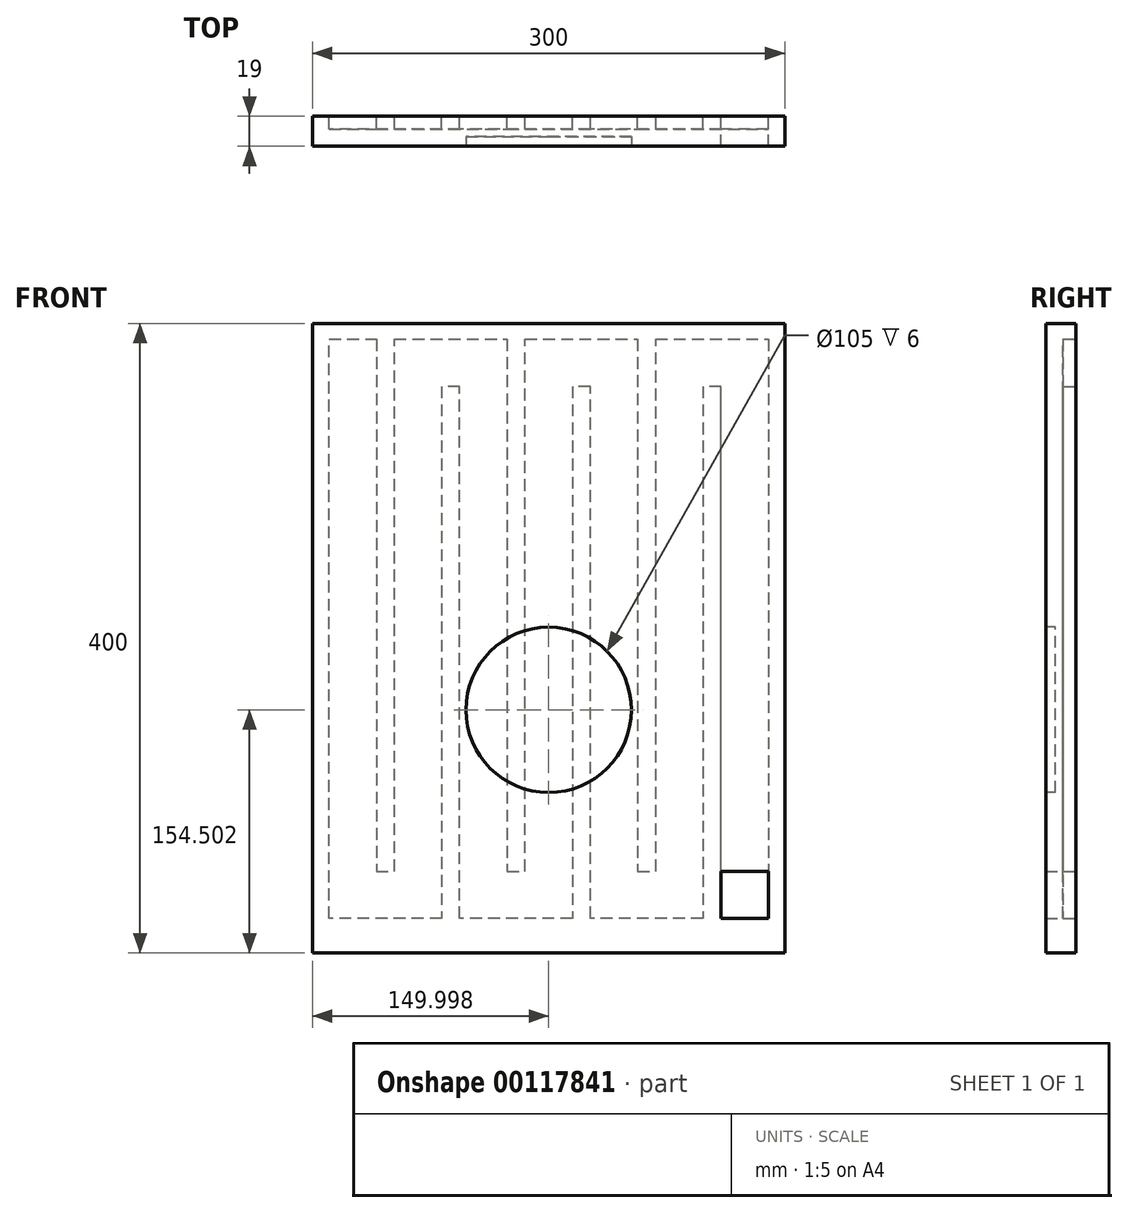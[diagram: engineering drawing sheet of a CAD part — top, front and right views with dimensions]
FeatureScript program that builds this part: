
annotation { "Feature Type Name" : "Feature", "Feature Type Description" : "" }
export const myFeature = defineFeature(function(context is Context, id is Id, definition is map)
    precondition{}
    {
        {
            var Q0;
            Q0=qCreatedBy(makeId("Front.planeOp"),FACE);
            var sketch = newSketch(context, id + "F0", { "sketchPlane" : qUnion([Q0])});
            skLineSegment(sketch, "E0.bottom", {"start": v(-198.08, 243.93) * mm, "end": v(101.92, 243.93) * mm});
            skLineSegment(sketch, "E0.top", {"start": v(-198.08, -156.07) * mm, "end": v(101.92, -156.07) * mm});
            skLineSegment(sketch, "E0.left", {"start": v(-198.08, 243.93) * mm, "end": v(-198.08, -156.07) * mm});
            skLineSegment(sketch, "E0.right", {"start": v(101.92, 243.93) * mm, "end": v(101.92, -156.07) * mm});
            skSolve(sketch);
        }
        {
            var Q0;
            Q0 = qSketchRegion(id + "F0", true);
            extrude(context, id + "F1", {"entities" : qUnion([Q0]), "depth" : 19 * mm});
        }
        {
            var Q0;
            Q0=makeQuery(id+"F1.opExtrude","CAP_FACE",FACE,{"disambiguationData":[OSD([sQuery(id+"F0.wireOp",EDGE,"E0.bottom"),sQuery(id+"F0.wireOp",EDGE,"E0.top"),sQuery(id+"F0.wireOp",EDGE,"E0.left"),sQuery(id+"F0.wireOp",EDGE,"E0.right")])],"isStart":false});
            var sketch = newSketch(context, id + "F2", { "sketchPlane" : qUnion([Q0])});
            skCircle(sketch, "E1", {"center": v(-48.08, -1.57) * mm, "radius": 52.5 * mm});
            skPoint(sketch, "E1.centerSnap0", {"position": v(-48.08, -156.07) * mm});
            skSolve(sketch);
        }
        {
            var Q0;
            Q0=makeQuery(id+"F2.imprint","IMPRINT",FACE,{"disambiguationData":[TD([[makeQuery(id+"F2.imprint","IMPRINT",EDGE,{"derivedFrom":sQuery(id+"F2.wireOp",EDGE,"E1")}),1.0]])]});
            extrude(context, id + "F3", {"entities" : qUnion([Q0]), "operationType" : NewBodyOperationType.REMOVE, "oppositeDirection" : true, "depth" : 6 * mm});
        }
        {
            var Q0;
            Q0=makeQuery(id+"F1.opExtrude","CAP_FACE",FACE,{"disambiguationData":[OSD([sQuery(id+"F0.wireOp",EDGE,"E0.bottom"),sQuery(id+"F0.wireOp",EDGE,"E0.top"),sQuery(id+"F0.wireOp",EDGE,"E0.left"),sQuery(id+"F0.wireOp",EDGE,"E0.right")])],"isStart":true});
            var sketch = newSketch(context, id + "F4", { "sketchPlane" : qUnion([Q0])});
            skLineSegment(sketch, "E2", {"start": v(-91.42, -134.07) * mm, "end": v(-61.42, -134.07) * mm});
            skLineSegment(sketch, "E3", {"start": v(-61.42, -134.07) * mm, "end": v(-61.42, 203.93) * mm});
            skLineSegment(sketch, "E4", {"start": v(-61.42, 203.93) * mm, "end": v(-49.92, 203.93) * mm});
            skLineSegment(sketch, "E5", {"start": v(-49.92, 203.93) * mm, "end": v(-49.92, -134.07) * mm});
            skLineSegment(sketch, "E6", {"start": v(-49.92, -134.07) * mm, "end": v(21.58, -134.07) * mm});
            skLineSegment(sketch, "E7", {"start": v(21.58, -134.07) * mm, "end": v(21.58, 203.93) * mm});
            skLineSegment(sketch, "E8", {"start": v(21.58, 203.93) * mm, "end": v(33.08, 203.93) * mm});
            skLineSegment(sketch, "E9", {"start": v(33.08, 203.93) * mm, "end": v(33.08, -134.07) * mm});
            skLineSegment(sketch, "E10", {"start": v(33.08, -134.07) * mm, "end": v(104.58, -134.07) * mm});
            skLineSegment(sketch, "E11", {"start": v(104.58, -134.07) * mm, "end": v(104.58, 203.93) * mm});
            skLineSegment(sketch, "E12", {"start": v(104.58, 203.93) * mm, "end": v(116.08, 203.93) * mm});
            skLineSegment(sketch, "E13", {"start": v(116.08, 203.93) * mm, "end": v(116.08, -134.07) * mm});
            skLineSegment(sketch, "E14", {"start": v(116.08, -134.07) * mm, "end": v(187.58, -134.07) * mm});
            skLineSegment(sketch, "E15", {"start": v(187.58, -134.07) * mm, "end": v(187.58, 233.93) * mm});
            skLineSegment(sketch, "E16", {"start": v(187.58, 233.93) * mm, "end": v(157.58, 233.93) * mm});
            skLineSegment(sketch, "E17", {"start": v(157.58, 233.93) * mm, "end": v(157.58, -104.07) * mm});
            skLineSegment(sketch, "E18", {"start": v(157.58, -104.07) * mm, "end": v(146.08, -104.07) * mm});
            skLineSegment(sketch, "E19", {"start": v(146.08, -104.07) * mm, "end": v(146.08, 233.93) * mm});
            skLineSegment(sketch, "E20", {"start": v(146.08, 233.93) * mm, "end": v(74.58, 233.93) * mm});
            skLineSegment(sketch, "E21", {"start": v(74.58, 233.93) * mm, "end": v(74.58, -104.07) * mm});
            skLineSegment(sketch, "E22", {"start": v(74.58, -104.07) * mm, "end": v(63.08, -104.07) * mm});
            skLineSegment(sketch, "E23", {"start": v(63.08, -104.07) * mm, "end": v(63.08, 233.93) * mm});
            skLineSegment(sketch, "E24", {"start": v(63.08, 233.93) * mm, "end": v(-8.42, 233.93) * mm});
            skLineSegment(sketch, "E25", {"start": v(-8.42, 233.93) * mm, "end": v(-8.42, -104.07) * mm});
            skLineSegment(sketch, "E26", {"start": v(-8.42, -104.07) * mm, "end": v(-19.92, -104.07) * mm});
            skLineSegment(sketch, "E27", {"start": v(-19.92, -104.07) * mm, "end": v(-19.92, 233.93) * mm});
            skLineSegment(sketch, "E28", {"start": v(-19.92, 233.93) * mm, "end": v(-91.42, 233.93) * mm});
            skLineSegment(sketch, "E29", {"start": v(-91.42, 233.93) * mm, "end": v(-91.42, -134.07) * mm});
            skSolve(sketch);
        }
        {
            var Q0;
            Q0 = qSketchRegion(id + "F4", true);
            extrude(context, id + "F5", {"entities" : qUnion([Q0]), "operationType" : NewBodyOperationType.REMOVE, "oppositeDirection" : true, "depth" : 8 * mm});
        }
        {
            var Q0;
            Q0=makeQuery(id+"F5.boolean.opBoolean","COPY",FACE,{"derivedFrom":makeQuery(id+"F5.opExtrude","CAP_FACE",FACE,{"disambiguationData":[OSD([sQuery(id+"F4.wireOp",EDGE,"E2"),sQuery(id+"F4.wireOp",EDGE,"E3"),sQuery(id+"F4.wireOp",EDGE,"E4"),sQuery(id+"F4.wireOp",EDGE,"E5"),sQuery(id+"F4.wireOp",EDGE,"E6"),sQuery(id+"F4.wireOp",EDGE,"E7"),sQuery(id+"F4.wireOp",EDGE,"E8"),sQuery(id+"F4.wireOp",EDGE,"E9"),sQuery(id+"F4.wireOp",EDGE,"E10"),sQuery(id+"F4.wireOp",EDGE,"E11"),sQuery(id+"F4.wireOp",EDGE,"E12"),sQuery(id+"F4.wireOp",EDGE,"E13"),sQuery(id+"F4.wireOp",EDGE,"E14"),sQuery(id+"F4.wireOp",EDGE,"E15"),sQuery(id+"F4.wireOp",EDGE,"E16"),sQuery(id+"F4.wireOp",EDGE,"E17"),sQuery(id+"F4.wireOp",EDGE,"E18"),sQuery(id+"F4.wireOp",EDGE,"E19"),sQuery(id+"F4.wireOp",EDGE,"E20"),sQuery(id+"F4.wireOp",EDGE,"E21"),sQuery(id+"F4.wireOp",EDGE,"E22"),sQuery(id+"F4.wireOp",EDGE,"E23"),sQuery(id+"F4.wireOp",EDGE,"E24"),sQuery(id+"F4.wireOp",EDGE,"E25"),sQuery(id+"F4.wireOp",EDGE,"E26"),sQuery(id+"F4.wireOp",EDGE,"E27"),sQuery(id+"F4.wireOp",EDGE,"E28"),sQuery(id+"F4.wireOp",EDGE,"E29")])],"isStart":false})});
            var sketch = newSketch(context, id + "F6", { "sketchPlane" : qUnion([Q0])});
            skLineSegment(sketch, "E30.bottom", {"start": v(-91.42, -104.07) * mm, "end": v(-61.42, -104.07) * mm});
            skLineSegment(sketch, "E30.top", {"start": v(-91.42, -134.07) * mm, "end": v(-61.42, -134.07) * mm});
            skLineSegment(sketch, "E30.left", {"start": v(-91.42, -104.07) * mm, "end": v(-91.42, -134.07) * mm});
            skLineSegment(sketch, "E30.right", {"start": v(-61.42, -104.07) * mm, "end": v(-61.42, -134.07) * mm});
            skSolve(sketch);
        }
        {
            var Q0;
            Q0 = qSketchRegion(id + "F6", true);
            extrude(context, id + "F7", {"entities" : qUnion([Q0]), "operationType" : NewBodyOperationType.REMOVE, "oppositeDirection" : true, "depth" : 11 * mm});
        }
    });
